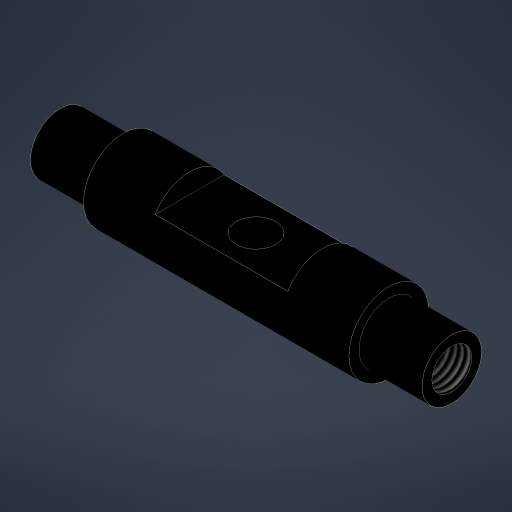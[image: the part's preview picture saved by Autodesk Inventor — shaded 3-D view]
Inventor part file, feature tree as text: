
AUTODESK INVENTOR PART (.ipt)
format: ipt  version: 2024.1 (Build 281209000, 209)  size: 216,064 bytes
history: native  units: mm
features: extrude x7, sketch x4, thread x2
ambient origin geometry x8: Origin, YZ Plane, XZ Plane, XY Plane, X Axis, Y Axis, Z Axis, Center Point
bodies: Solid1 (feature_tree)
feature tree (13):
  extrude  "Extrusion1"  Depth=29.5mm TaperAngle=0.0deg
  extrude  "Extrusion2"  Depth=3.0mm
  extrude  "Extrusion3"  Depth=4.5mm
  extrude  "Extrusion4"  Depth=3.0mm
  extrude  "Extrusion5"  Depth=3.0mm TaperAngle=0.0deg
  thread  "Thread1"  [1 undecoded]
  thread  "Thread2"  [1 undecoded]
  extrude  "Extrusion6"  Depth=10.0mm TaperAngle=0.0deg
  extrude  "Extrusion7"  Depth=3.0mm
  sketch  "Sketch2"  dims[d0=6.0mm d1=29.5mm d2=0.0mm]
  sketch  "Sketch4"  dims[d3=4.5mm d4=3.0mm]
  sketch  "Sketch6"  dims[d5=4.75mm d6=0.0mm d7=4.5mm]
  sketch  "Sketch7"  dims[d8=3.0mm d9=6.0mm d10=4.75mm d11=0.0mm d12=1.5mm d13=7.0mm d14=10.0mm d15=0.0mm d16=3.0mm d17=0.0mm d18=0.0mm d19=4.75mm d20=0.0mm d21=4.75mm d22=0.0mm d23=2.0mm d24=0.0mm d25=2.0mm d26=0.0mm]
note: 2 required parameter values undecoded (feature->parameter linkage not recoverable at this tier; creation-order binding heuristic only, values carry confidence <= 0.55)
